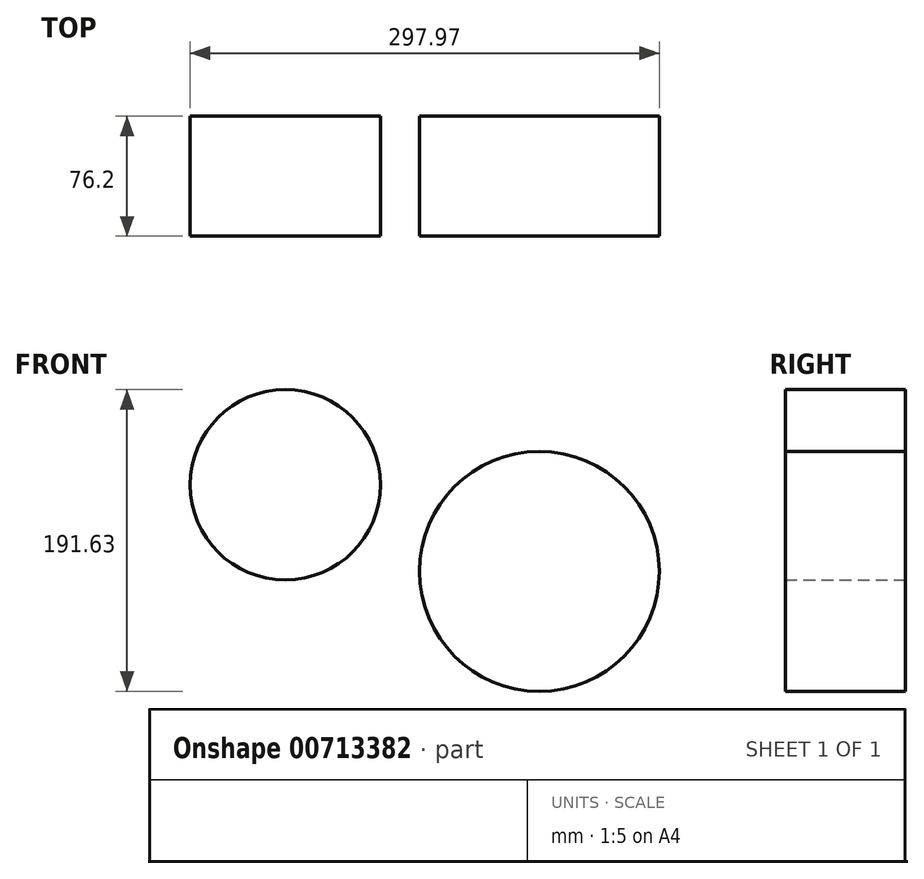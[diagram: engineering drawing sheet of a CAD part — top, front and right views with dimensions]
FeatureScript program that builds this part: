
annotation { "Feature Type Name" : "Feature", "Feature Type Description" : "" }
export const myFeature = defineFeature(function(context is Context, id is Id, definition is map)
    precondition{}
    {
        {
            var Q0;
            Q0=qCreatedBy(makeId("Front.planeOp"),FACE);
            var sketch = newSketch(context, id + "F0", { "sketchPlane" : qUnion([Q0])});
            skCircle(sketch, "E0", {"center": v(-91.08, 14.36) * mm, "radius": 60.44 * mm});
            skCircle(sketch, "E1", {"center": v(70.25, -40.63) * mm, "radius": 76.2 * mm});
            skSolve(sketch);
        }
        {
            var Q0;
            Q0=makeQuery(id+"F0.imprint","IMPRINT",FACE,{"disambiguationData":[TD([[makeQuery(id+"F0.imprint","IMPRINT",EDGE,{"derivedFrom":sQuery(id+"F0.wireOp",EDGE,"E1")}),1.0]])]});
            var Q1;
            Q1=makeQuery(id+"F0.imprint","IMPRINT",FACE,{"disambiguationData":[TD([[makeQuery(id+"F0.imprint","IMPRINT",EDGE,{"derivedFrom":sQuery(id+"F0.wireOp",EDGE,"E0")}),1.0]])]});
            var Q2;
            Q2=sQuery(id+"F0.wireOp",EDGE,"E1");
            var Q3;
            Q3=sQuery(id+"F0.wireOp",EDGE,"E0");
            extrude(context, id + "F1", {"entities" : qUnion([Q0, Q1]), "surfaceEntities" : qUnion([Q2, Q3]), "depth" : 76.2 * mm, "offsetDistance" : 25.4 * mm});
        }
        {
            var Q0;
            Q0=makeQuery(id+"F1.opExtrude","CAP_FACE",FACE,{"disambiguationData":[OSD([sQuery(id+"F0.wireOp",EDGE,"E0")])],"isStart":false});
            var sketch = newSketch(context, id + "F2", { "sketchPlane" : qUnion([Q0])});
            skCircle(sketch, "E2", {"center": v(-91.08, 14.36) * mm, "radius": 12.7 * mm});
            skSolve(sketch);
        }
        {
            var Q0;
            Q0 = qSketchRegion(id + "F2", true);
            var Q1;
            Q1=sQuery(id+"F2.wireOp",EDGE,"E2");
            extrude(context, id + "F3", {"entities" : qUnion([Q0]), "bodyType" : ToolBodyType.SURFACE, "surfaceEntities" : qUnion([Q1]), "depth" : 25.4 * mm, "offsetDistance" : 25.4 * mm});
        }
    });
